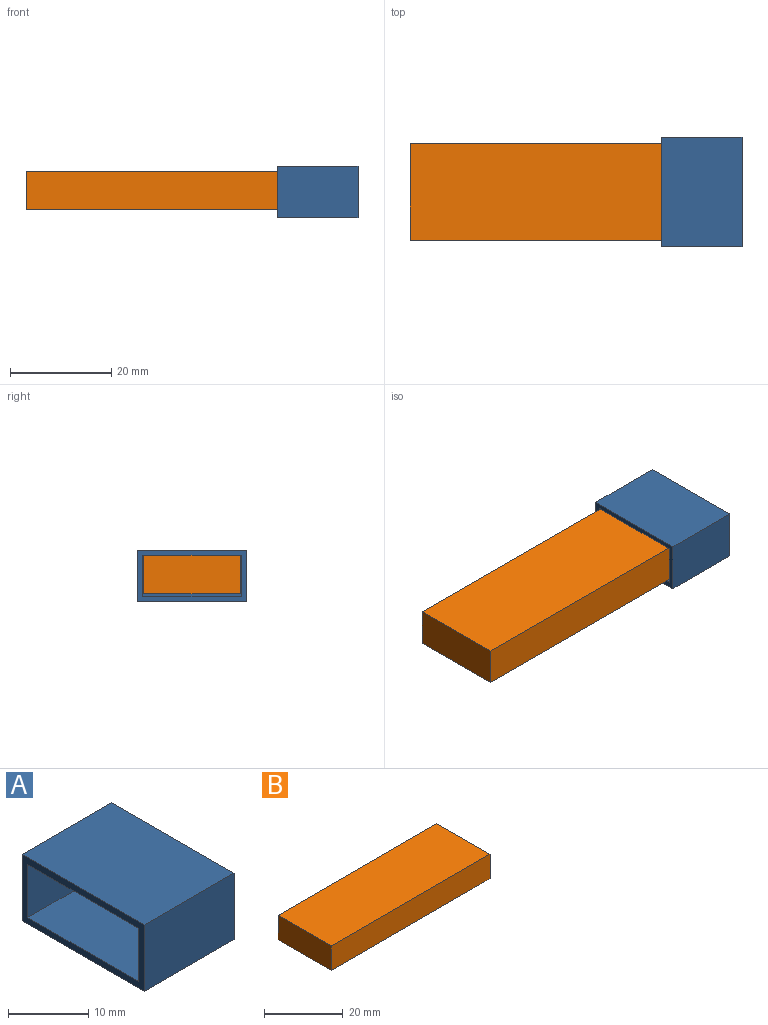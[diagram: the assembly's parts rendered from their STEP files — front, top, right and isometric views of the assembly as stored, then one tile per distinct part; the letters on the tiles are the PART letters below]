
ASSEMBLY  parts=2 mates=1
PART A: 11 faces, bbox 15.9x21.6x10.2 mm
  f0: plane 21.59x10.16mm, normal (1,0,0), area 219.4mm2, adj f1,f3,f4,f5
  f1: plane 15.88x10.16mm, normal (0,1,0), area 161.3mm2, adj f0,f2,f4,f5
  f2: plane 21.59x10.16mm, normal (-1,0,0), area 60.4mm2, adj f1,f3,f4,f5,f6,f7,f8,f9
  f3: plane 15.88x10.16mm, normal (0,-1,0), area 161.3mm2, adj f0,f2,f4,f5
  f4: plane 21.59x15.88mm, normal (0,0,1), area 342.7mm2, adj f0,f1,f2,f3
  f5: plane 21.59x15.88mm, normal (0,0,-1), area 342.7mm2, adj f0,f1,f2,f3
  f6: plane 19.56x14.61mm, normal (0,0,1), area 285.6mm2, adj f2,f7,f9,f10
  f7: plane 14.61x8.13mm, normal (0,1,0), area 118.7mm2, adj f2,f6,f8,f10
  f8: plane 19.56x14.61mm, normal (0,0,-1), area 285.6mm2, adj f2,f7,f9,f10
  f9: plane 14.61x8.13mm, normal (0,-1,0), area 118.7mm2, adj f2,f6,f8,f10
  f10: plane 19.56x8.13mm, normal (-1,0,0), area 159mm2, adj f6,f7,f8,f9
PART B: 11 faces, bbox 57.2x19.1x7.6 mm
  f0: plane 19.05x7.62mm, normal (1,0,0), area 44.4mm2, adj f2,f3,f4,f5,f6,f7,f8,f9
  f1: plane 19.05x7.62mm, normal (-1,0,0), area 145.2mm2, adj f2,f3,f4,f5
  f2: plane 57.15x7.62mm, normal (0,-1,0), area 435.5mm2, adj f0,f1,f4,f5
  f3: plane 57.15x7.62mm, normal (0,1,0), area 435.5mm2, adj f0,f1,f4,f5
  f4: plane 57.15x19.05mm, normal (0,0,1), area 1088.7mm2, adj f0,f1,f2,f3
  f5: plane 57.15x19.05mm, normal (0,0,-1), area 1088.7mm2, adj f0,f1,f2,f3
  f6: plane 55.88x15.88mm, normal (0,0,1), area 887.1mm2, adj f0,f7,f9,f10
  f7: plane 55.88x6.35mm, normal (0,-1,0), area 354.8mm2, adj f0,f6,f8,f10
  f8: plane 55.88x15.88mm, normal (0,0,-1), area 887.1mm2, adj f0,f7,f9,f10
  f9: plane 55.88x6.35mm, normal (0,1,0), area 354.8mm2, adj f0,f6,f8,f10
  f10: plane 15.88x6.35mm, normal (1,0,0), area 100.8mm2, adj f6,f7,f8,f9
PLACE A t=(-70.13,-15.34,-1.52)mm
PLACE B t=(-30.3,-16.61,0)mm
MATE slider A.f8 <-> B.f4  axis (0,0,-1) through (-30.82,-9.43,7.62)mm
